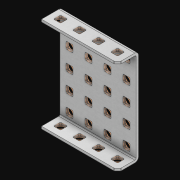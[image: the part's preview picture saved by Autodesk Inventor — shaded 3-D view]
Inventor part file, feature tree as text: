
AUTODESK INVENTOR PART (.ipt)
format: ipt  version: 2021 (Build 250183000, 183)  size: 2,829,824 bytes
history: native  units: in
note: dims shown in document units (in); Inventor stores cm internally (conversion verified against a paired STEP export)
features: extrude x29, other x28, sketch x4, thicken_offset x3, pattern_linear x3, imported_body x1
ambient origin geometry x8: Origin, YZ Plane, XZ Plane, XY Plane, X Axis, Y Axis, Z Axis, Center Point
bodies: Solid1 (feature_tree)
feature tree (68):
  thicken_offset  "Thicken1"
  thicken_offset  "Thicken2"
  thicken_offset  "Thicken3"
  pattern_linear  "Rectangular Pattern1"  Spacing1=0.001in  [1 undecoded]
  pattern_linear  "Rectangular Pattern2"  Spacing1=0.001in  [1 undecoded]
  pattern_linear  "Rectangular Pattern3"  Spacing1=0.182in  [1 undecoded]
  extrude  "Extrusion1"  Depth=0.063in TaperAngle=0.0deg
  sketch  "Sketch1"  dims[d0=0.001in]
  other  "Srf1"
  sketch  "Sketch2"  dims[d1=0.001in]
  other  "Srf2"
  sketch  "Sketch3"  dims[d2=0.001in]
  other  "Srf3"
  other  "Srf4"
  other  "Srf5"
  other  "Srf6"
  other  "Srf38"
  other  "Srf39"
  other  "Srf40"
  other  "Srf72"
  other  "Srf73"
  other  "Srf74"
  other  "Srf106"
  other  "Srf107"
  other  "Srf108"
  other  "Srf109"
  other  "Srf141"
  other  "Srf142"
  other  "Srf143"
  other  "Srf144"
  other  "Srf176"
  other  "Srf177"
  other  "Srf178"
  other  "Srf179"
  other  "Srf211"
  other  "Srf212"
  other  "Srf213"
  other  "Srf214"
  sketch  "Sketch4"  dims[d3=0.001in d4=0.001in d5=0.001in d6=0.182in d7=0.063in d8=0.0in d9=0.182in d10=0.063in d11=0.0in d12=0.182in d13=0.063in d14=0.0in d17=0.5in d18=1.5748in d20=0.5in d21=1.5748in d23=0.5in d24=1.9685in d26=0.5in d27=15.5in d28=0.0in]
  imported_body  "Imported1"
  extrude  "ExtrusionSrf1"  Depth=0.182in
  extrude  "ExtrusionSrf2"  Depth=0.063in TaperAngle=0.0deg
  extrude  "ExtrusionSrf3"  Depth=0.182in
  extrude  "ExtrusionSrf4"  Depth=0.063in TaperAngle=0.0deg
  extrude  "ExtrusionSrf5"  Depth=0.5in
  extrude  "ExtrusionSrf6"  Depth=0.5in
  extrude  "ExtrusionSrf38"  Depth=0.5in
  extrude  "ExtrusionSrf39"  Depth=0.5in
  extrude  "ExtrusionSrf40"  Depth=0.5in
  extrude  "ExtrusionSrf72"  Depth=0.5in
  extrude  "ExtrusionSrf73"  Depth=0.5in
  extrude  "ExtrusionSrf74"  TaperAngle=0.0deg  [1 undecoded]
  extrude  "ExtrusionSrf106"  [1 undecoded]
  extrude  "ExtrusionSrf107"  [1 undecoded]
  extrude  "ExtrusionSrf108"  [1 undecoded]
  extrude  "ExtrusionSrf109"  [1 undecoded]
  extrude  "ExtrusionSrf141"  [1 undecoded]
  extrude  "ExtrusionSrf142"  [1 undecoded]
  extrude  "ExtrusionSrf143"  [1 undecoded]
  extrude  "ExtrusionSrf144"  [1 undecoded]
  extrude  "ExtrusionSrf176"  [1 undecoded]
  extrude  "ExtrusionSrf177"  [1 undecoded]
  extrude  "ExtrusionSrf178"  [1 undecoded]
  extrude  "ExtrusionSrf179"  [1 undecoded]
  extrude  "ExtrusionSrf211"  [1 undecoded]
  extrude  "ExtrusionSrf212"  [1 undecoded]
  extrude  "ExtrusionSrf213"  [1 undecoded]
  extrude  "ExtrusionSrf214"  [1 undecoded]
note: 20 required parameter values undecoded (feature->parameter linkage not recoverable at this tier; creation-order binding heuristic only, values carry confidence <= 0.55)
